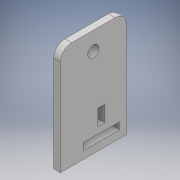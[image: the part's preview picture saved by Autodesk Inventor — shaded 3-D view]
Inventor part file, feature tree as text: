
AUTODESK INVENTOR PART (.ipt)
format: ipt  version: 2018 (Build 220112000, 112)  size: 125,952 bytes
history: native  units: mm
features: extrude x2, fillet x2, sketch x2, other x1
ambient origin geometry x8: Origin, YZ Plane, XZ Plane, XY Plane, X Axis, Y Axis, Z Axis, Center Point
bodies: Body1 (feature_tree)
feature tree (7):
  other  "Sólido1"
  extrude  "Extrusión1"  Depth=5.0mm
  extrude  "Extrusión2"  Depth=5.0mm
  fillet  "Empalme1"  Radius=5.0mm
  fillet  "Empalme2"  [1 undecoded]
  sketch  "Boceto1"  dims[d26=3.0mm d27=0.0mm d28=5.0mm]
  sketch  "Boceto2"  dims[d29=3.0mm d30=0.0mm d31=5.0mm d32=5.0mm]
note: 1 required parameter value undecoded (feature->parameter linkage not recoverable at this tier; creation-order binding heuristic only, values carry confidence <= 0.55)
